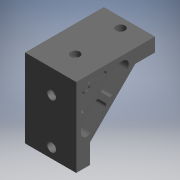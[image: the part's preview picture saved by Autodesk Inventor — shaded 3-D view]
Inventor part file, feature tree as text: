
AUTODESK INVENTOR PART (.ipt)
format: ipt  version: 2017.3 (Build 213256000, 256)  size: 255,488 bytes
history: native  units: mm (DEFAULTED — no unit token found)
features: other x63, sketch x5, revolve x3, extrude x1, hole x1
ambient origin geometry x8: Origin, YZ Plane, XZ Plane, XY Plane, X Axis, Y Axis, Z Axis, Center Point
bodies: Solid1 (feature_tree)
feature tree (73):
  extrude  "Extrusion1"  TaperAngle=360.0deg  [1 undecoded]
  revolve  "Revolution1"  Angle=360.0deg
  revolve  "Revolution2"  [1 undecoded]
  hole  "Hole1"  [1 undecoded]
  revolve  "Revolution3"  [1 undecoded]
  other  "bracket_to_dummy_XY"
  other  "bracket_to_dummy_YZ"
  other  "bracket_to_dummy_ZX"
  other  "bracket_to_dummy_X"
  other  "bracket_to_dummy_Y"
  other  "bracket_to_dummy_Z"
  other  "bracket_to_dummy_Center"
  other  "to_bolt_a_1_XY"
  other  "to_bolt_a_1_YZ"
  other  "to_bolt_a_1_ZX"
  other  "to_bolt_a_1_X"
  other  "to_bolt_a_1_Y"
  other  "to_bolt_a_1_Z"
  other  "to_bolt_a_1_Center"
  other  "to_bolt_b_1_XY"
  other  "to_bolt_b_1_YZ"
  other  "to_bolt_b_1_ZX"
  other  "to_bolt_b_1_X"
  other  "to_bolt_b_1_Y"
  other  "to_bolt_b_1_Z"
  other  "to_bolt_b_1_Center"
  other  "to_bolt_base_a_1_XY"
  other  "to_bolt_base_a_1_YZ"
  other  "to_bolt_base_a_1_ZX"
  other  "to_bolt_base_a_1_X"
  other  "to_bolt_base_a_1_Y"
  other  "to_bolt_base_a_1_Z"
  other  "to_bolt_base_a_1_Center"
  other  "to_bolt_base_b_1_XY"
  other  "to_bolt_base_b_1_YZ"
  other  "to_bolt_base_b_1_ZX"
  other  "to_bolt_base_b_1_X"
  other  "to_bolt_base_b_1_Y"
  other  "to_bolt_base_b_1_Z"
  other  "to_bolt_base_b_1_Center"
  other  "to_nut_a_1_XY"
  other  "to_nut_a_1_YZ"
  other  "to_nut_a_1_ZX"
  other  "to_nut_a_1_X"
  other  "to_nut_a_1_Y"
  other  "to_nut_a_1_Z"
  other  "to_nut_a_1_Center"
  other  "to_nut_a_3_XY"
  other  "to_nut_a_3_YZ"
  other  "to_nut_a_3_ZX"
  other  "to_nut_a_3_X"
  other  "to_nut_a_3_Y"
  other  "to_nut_a_3_Z"
  other  "to_nut_a_3_Center"
  other  "to_nut_base_a_1_XY"
  other  "to_nut_base_a_1_YZ"
  other  "to_nut_base_a_1_ZX"
  other  "to_nut_base_a_1_X"
  other  "to_nut_base_a_1_Y"
  other  "to_nut_base_a_1_Z"
  other  "to_nut_base_a_1_Center"
  other  "to_nut_base_a_3_XY"
  other  "to_nut_base_a_3_YZ"
  other  "to_nut_base_a_3_ZX"
  other  "to_nut_base_a_3_X"
  other  "to_nut_base_a_3_Y"
  other  "to_nut_base_a_3_Z"
  other  "to_nut_base_a_3_Center"
  sketch  "Sketch_2"  dims[d0=52.0mm d1=0.0mm d2=360.0deg]
  sketch  "Sketch_3"  dims[d3=360.0deg]
  sketch  "Sketch_4"  dims[d4=9.0mm d5=6.0mm d6=4.0mm d7=2.0mm d8=90.0deg d9=15.0mm d10=0.0mm d11=360.0deg]
  sketch  "Sketch4"  dims[d12=0.0mm d13=0.0mm d14=0.0mm d15=0.0mm d16=0.0mm]
  sketch  "Sketch_6"
note: 4 required parameter values undecoded (feature->parameter linkage not recoverable at this tier; creation-order binding heuristic only, values carry confidence <= 0.55)
